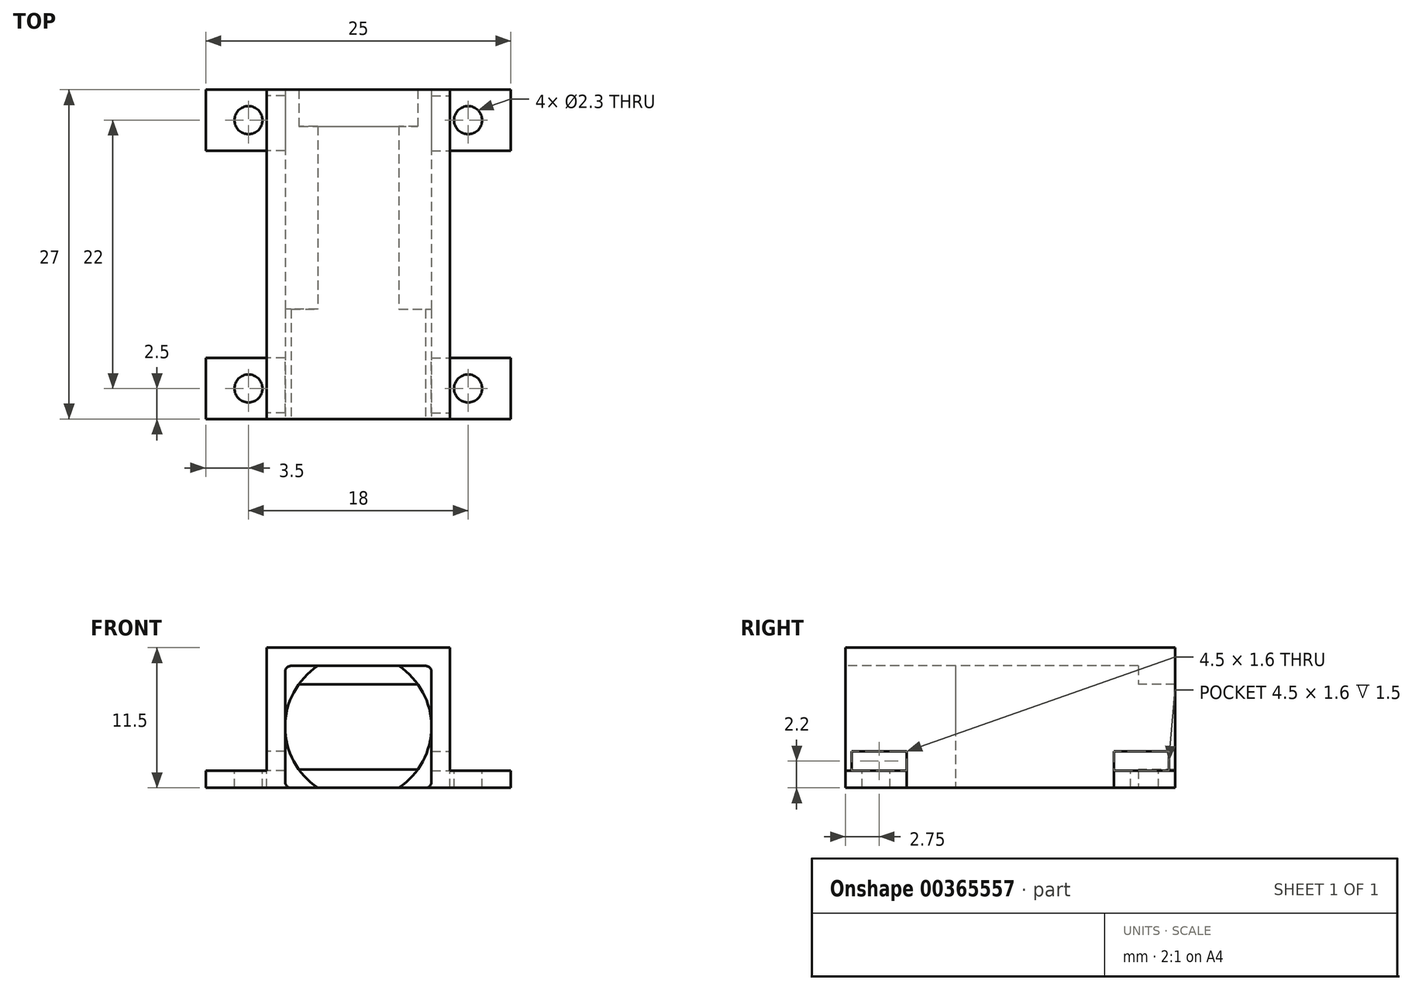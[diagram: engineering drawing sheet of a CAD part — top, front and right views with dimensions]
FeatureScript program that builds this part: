
annotation { "Feature Type Name" : "Feature", "Feature Type Description" : "" }
export const myFeature = defineFeature(function(context is Context, id is Id, definition is map)
    precondition{}
    {
        {
            var Q0;
            Q0=qCreatedBy(makeId("Front.planeOp"),FACE);
            var sketch = newSketch(context, id + "F0", { "sketchPlane" : qUnion([Q0])});
            skLineSegment(sketch, "E0", {"start": v(7.5, -5) * mm, "end": v(7.5, 6.5) * mm});
            skLineSegment(sketch, "E1", {"start": v(7.5, 6.5) * mm, "end": v(-7.5, 6.5) * mm});
            skLineSegment(sketch, "E2", {"start": v(-7.5, 6.5) * mm, "end": v(-7.5, -5) * mm});
            skPoint(sketch, "E3", {"position": v(0, -5) * mm});
            skLineSegment(sketch, "E4", {"start": v(-7.5, -5) * mm, "end": v(7.5, -5) * mm});
            skSolve(sketch);
        }
        {
            var Q0;
            Q0=makeQuery(id+"F0.imprint","IMPRINT",FACE,{"disambiguationData":[TD([[makeQuery(id+"F0.imprint","IMPRINT",EDGE,{"derivedFrom":sQuery(id+"F0.wireOp",EDGE,"E0")}),1.0]])]});
            extrude(context, id + "F1", {"entities" : qUnion([Q0]), "oppositeDirection" : true, "depth" : 27 * mm, "offsetDistance" : 25 * mm});
        }
        {
            var Q0;
            Q0=qCreatedBy(makeId("Front.planeOp"),FACE);
            var sketch = newSketch(context, id + "F2", { "sketchPlane" : qUnion([Q0])});
            skLineSegment(sketch, "E5.bottom", {"start": v(-5.5, 5) * mm, "end": v(5.5, 5) * mm});
            skLineSegment(sketch, "E5.top", {"start": v(-5.5, -5) * mm, "end": v(5.5, -5) * mm});
            skLineSegment(sketch, "E5.left", {"start": v(-6, 4.5) * mm, "end": v(-6, -4.5) * mm});
            skLineSegment(sketch, "E5.right", {"start": v(6, 4.5) * mm, "end": v(6, -4.5) * mm});
            skPoint(sketch, "E5.middle", {"position": v(0, 0) * mm});
            skPoint(sketch, "E6.visualSharp", {"position": v(-6, 5) * mm});
            skArc(sketch, "E6.filletArc", {"start": v(-5.5, 5) * mm, "mid": v(-5.85, 4.85) * mm, "end": v(-6, 4.5) * mm});
            skPoint(sketch, "E7.visualSharp", {"position": v(6, 5) * mm});
            skArc(sketch, "E7.filletArc", {"start": v(6, 4.5) * mm, "mid": v(5.85, 4.85) * mm, "end": v(5.5, 5) * mm});
            skPoint(sketch, "E8.visualSharp", {"position": v(6, -5) * mm});
            skArc(sketch, "E8.filletArc", {"start": v(5.5, -5) * mm, "mid": v(5.85, -4.85) * mm, "end": v(6, -4.5) * mm});
            skPoint(sketch, "E9.visualSharp", {"position": v(-6, -5) * mm});
            skArc(sketch, "E9.filletArc", {"start": v(-6, -4.5) * mm, "mid": v(-5.85, -4.85) * mm, "end": v(-5.5, -5) * mm});
            skSolve(sketch);
        }
        {
            var Q0;
            Q0=makeQuery(id+"F2.imprint","IMPRINT",FACE,{"disambiguationData":[TD([[makeQuery(id+"F2.imprint","IMPRINT",EDGE,{"derivedFrom":sQuery(id+"F2.wireOp",EDGE,"E5.bottom")}),-1.0]])]});
            extrude(context, id + "F3", {"entities" : qUnion([Q0]), "operationType" : NewBodyOperationType.REMOVE, "oppositeDirection" : true, "depth" : 9 * mm, "offsetDistance" : 25 * mm});
        }
        {
            var Q0;
            Q0=makeQuery(id+"F3.boolean.opBoolean","COPY",FACE,{"derivedFrom":makeQuery(id+"F3.opExtrude","CAP_FACE",FACE,{"disambiguationData":[OSD([sQuery(id+"F2.wireOp",EDGE,"E5.bottom"),sQuery(id+"F2.wireOp",EDGE,"E5.top"),sQuery(id+"F2.wireOp",EDGE,"E5.left"),sQuery(id+"F2.wireOp",EDGE,"E5.right"),sQuery(id+"F2.wireOp",EDGE,"E6.filletArc"),sQuery(id+"F2.wireOp",EDGE,"E7.filletArc"),sQuery(id+"F2.wireOp",EDGE,"E8.filletArc"),sQuery(id+"F2.wireOp",EDGE,"E9.filletArc")])],"isStart":false})});
            var sketch = newSketch(context, id + "F4", { "sketchPlane" : qUnion([Q0])});
            skArc(sketch, "E10", {"start": v(3.32, -5) * mm, "mid": v(6, 0) * mm, "end": v(3.32, 5) * mm});
            skLineSegment(sketch, "E11", {"start": v(0, 0) * mm, "end": v(0, 5) * mm});
            skLineSegment(sketch, "E12", {"start": v(-3.32, 5) * mm, "end": v(3.32, 5) * mm});
            skLineSegment(sketch, "E13.MirrorCS", {"start": v(-3.32, -5) * mm, "end": v(3.32, -5) * mm});
            skArc(sketch, "E14.trimOffspring", {"start": v(-3.32, 5) * mm, "mid": v(-6, 0) * mm, "end": v(-3.32, -5) * mm});
            skSolve(sketch);
        }
        {
            var Q0;
            {var subQ2=makeQuery(id+"F3.opExtrude","CAP_EDGE",EDGE,{"disambiguationData":[OSD([sQuery(id+"F2.wireOp",EDGE,"E5.top")])],"isStart":false});var subQ6=sQuery(id+"F4.wireOp",EDGE,"E10");var subQ7=makeQuery(id+"F4.imprint","INTERSECT",VERTEX,{"derivedFrom":[subQ2,subQ6]});Q0=makeQuery(id+"F4.imprint","IMPRINT",FACE,{"disambiguationData":[TD([[makeQuery(id+"F4.imprint","IMPRINT",EDGE,{"disambiguationData":[TD([[subQ7,-1.0]])],"derivedFrom":subQ6}),1.0]])]});}
            var Q1;
            {var subQ0=sQuery(id+"F4.wireOp",EDGE,"E13.MirrorCS");Q1=makeQuery(id+"F4.imprint","IMPRINT",FACE,{"disambiguationData":[TD([[makeQuery(id+"F4.imprint","IMPRINT",EDGE,{"derivedFrom":subQ0}),1.0]])]});}
            var Q2;
            {var subQ0=sQuery(id+"F4.wireOp",EDGE,"E12");var subQ1=sQuery(id+"F4.wireOp",EDGE,"E10");var subQ2=makeQuery(id+"F4.imprint","INTERSECT",VERTEX,{"derivedFrom":[subQ1,subQ0]});Q2=makeQuery(id+"F4.imprint","IMPRINT",FACE,{"disambiguationData":[TD([[makeQuery(id+"F4.imprint","IMPRINT",EDGE,{"disambiguationData":[TD([[subQ2,1.0]])],"derivedFrom":subQ1}),1.0]])]});}
            var Q3;
            {var subQ0=sQuery(id+"F4.wireOp",EDGE,"E12");var subQ1=sQuery(id+"F4.wireOp",EDGE,"E11");var subQ2=makeQuery(id+"F4.imprint","INTERSECT",VERTEX,{"derivedFrom":[subQ1,subQ0]});Q3=makeQuery(id+"F4.imprint","IMPRINT",FACE,{"disambiguationData":[TD([[makeQuery(id+"F4.imprint","IMPRINT",EDGE,{"disambiguationData":[TD([[subQ2,1.0]])],"derivedFrom":subQ1}),1.0]])]});}
            extrude(context, id + "F5", {"entities" : qUnion([Q0, Q1, Q2, Q3]), "operationType" : NewBodyOperationType.REMOVE, "oppositeDirection" : true, "depth" : 15 * mm, "offsetDistance" : 25 * mm});
        }
        {
            var Q0;
            Q0=makeQuery(id+"F5.boolean.opBoolean","COPY",FACE,{"derivedFrom":makeQuery(id+"F5.opExtrude","CAP_FACE",FACE,{"disambiguationData":[OSD([sQuery(id+"F4.wireOp",EDGE,"E10"),sQuery(id+"F4.wireOp",EDGE,"E12"),sQuery(id+"F4.wireOp",EDGE,"E13.MirrorCS"),sQuery(id+"F4.wireOp",EDGE,"E14.trimOffspring")])],"isStart":false})});
            var sketch = newSketch(context, id + "F6", { "sketchPlane" : qUnion([Q0])});
            skCircle(sketch, "E15", {"center": v(0, 0) * mm, "radius": 6 * mm});
            skLineSegment(sketch, "E16", {"start": v(0, 0) * mm, "end": v(0, 3.5) * mm});
            skPoint(sketch, "E16.endSnap0", {"position": v(0, 5) * mm});
            skLineSegment(sketch, "E17", {"start": v(-4.87, 3.5) * mm, "end": v(4.87, 3.5) * mm});
            skLineSegment(sketch, "E18.MirrorCS", {"start": v(-4.87, -3.5) * mm, "end": v(4.87, -3.5) * mm});
            skSolve(sketch);
        }
        {
            var Q0;
            {var subQ5=sQuery(id+"F6.wireOp",EDGE,"E18.MirrorCS");Q0=makeQuery(id+"F6.imprint","IMPRINT",FACE,{"disambiguationData":[TD([[makeQuery(id+"F6.imprint","IMPRINT",EDGE,{"derivedFrom":subQ5}),1.0]])]});}
            extrude(context, id + "F7", {"entities" : qUnion([Q0]), "operationType" : NewBodyOperationType.REMOVE, "oppositeDirection" : true, "depth" : 3 * mm, "offsetDistance" : 25 * mm});
        }
        {
            var Q0;
            Q0=makeQuery(id+"F1.opExtrude","SWEPT_FACE",FACE,{"disambiguationData":[OSD([sQuery(id+"F0.wireOp",EDGE,"E0")])]});
            var sketch = newSketch(context, id + "F8", { "sketchPlane" : qUnion([Q0])});
            skLineSegment(sketch, "E19.bottom", {"start": v(0, -5) * mm, "end": v(5, -5) * mm});
            skLineSegment(sketch, "E19.top", {"start": v(0, -3.6) * mm, "end": v(5, -3.6) * mm});
            skLineSegment(sketch, "E19.left", {"start": v(0, -5) * mm, "end": v(0, -3.6) * mm});
            skLineSegment(sketch, "E19.right", {"start": v(5, -5) * mm, "end": v(5, -3.6) * mm});
            skLineSegment(sketch, "E20.bottom", {"start": v(27, -5) * mm, "end": v(22, -5) * mm});
            skLineSegment(sketch, "E20.top", {"start": v(27, -3.6) * mm, "end": v(22, -3.6) * mm});
            skLineSegment(sketch, "E20.left", {"start": v(27, -5) * mm, "end": v(27, -3.6) * mm});
            skLineSegment(sketch, "E20.right", {"start": v(22, -5) * mm, "end": v(22, -3.6) * mm});
            skSolve(sketch);
        }
        {
            var Q0;
            Q0=makeQuery(id+"F8.imprint","IMPRINT",FACE,{"disambiguationData":[TD([[makeQuery(id+"F8.imprint","IMPRINT",EDGE,{"derivedFrom":sQuery(id+"F8.wireOp",EDGE,"E19.bottom")}),-1.0]])]});
            var Q1;
            Q1=makeQuery(id+"F8.imprint","IMPRINT",FACE,{"disambiguationData":[TD([[makeQuery(id+"F8.imprint","IMPRINT",EDGE,{"derivedFrom":sQuery(id+"F8.wireOp",EDGE,"E20.bottom")}),-1.0]])]});
            extrude(context, id + "F9", {"entities" : qUnion([Q0, Q1]), "operationType" : NewBodyOperationType.ADD, "depth" : 5 * mm, "offsetDistance" : 25 * mm});
        }
        {
            var Q0;
            Q0=makeQuery(id+"F9.opExtrude","SWEPT_FACE",FACE,{"disambiguationData":[OSD([sQuery(id+"F8.wireOp",EDGE,"E20.top")])]});
            var sketch = newSketch(context, id + "F10", { "sketchPlane" : qUnion([Q0])});
            skPoint(sketch, "E21", {"position": v(7.5, 24.5) * mm});
            skLineSegment(sketch, "E22", {"start": v(7.5, 24.5) * mm, "end": v(9, 24.5) * mm, "construction": true});
            skPoint(sketch, "E22.endSnap0", {"position": v(12.5, 24.5) * mm});
            skCircle(sketch, "E23", {"center": v(9, 24.5) * mm, "radius": 1.15 * mm});
            skLineSegment(sketch, "E24", {"start": v(9, 24.5) * mm, "end": v(9, 2.5) * mm, "construction": true});
            skCircle(sketch, "E25", {"center": v(9, 2.5) * mm, "radius": 1.15 * mm});
            skSolve(sketch);
        }
        {
            var Q0;
            Q0=makeQuery(id+"F10.imprint","IMPRINT",FACE,{"disambiguationData":[TD([[makeQuery(id+"F10.imprint","IMPRINT",EDGE,{"derivedFrom":sQuery(id+"F10.wireOp",EDGE,"E23")}),1.0]])]});
            var Q1;
            Q1=makeQuery(id+"F10.imprint","IMPRINT",FACE,{"disambiguationData":[TD([[makeQuery(id+"F10.imprint","IMPRINT",EDGE,{"derivedFrom":sQuery(id+"F10.wireOp",EDGE,"E25")}),1.0]])]});
            extrude(context, id + "F11", {"entities" : qUnion([Q0, Q1]), "operationType" : NewBodyOperationType.REMOVE, "oppositeDirection" : true, "depth" : 1.4 * mm, "offsetDistance" : 25 * mm});
        }
        {
            var Q0;
            Q0=makeQuery(id+"F1.opExtrude","SWEPT_FACE",FACE,{"disambiguationData":[OSD([sQuery(id+"F0.wireOp",EDGE,"E0")])]});
            var sketch = newSketch(context, id + "F12", { "sketchPlane" : qUnion([Q0])});
            skLineSegment(sketch, "E26.bottom", {"start": v(0.5, -3.6) * mm, "end": v(5, -3.6) * mm});
            skLineSegment(sketch, "E26.top", {"start": v(0.5, -2) * mm, "end": v(5, -2) * mm});
            skLineSegment(sketch, "E26.left", {"start": v(0.5, -3.6) * mm, "end": v(0.5, -2) * mm});
            skLineSegment(sketch, "E26.right", {"start": v(5, -3.6) * mm, "end": v(5, -2) * mm});
            skLineSegment(sketch, "E27.bottom", {"start": v(22, -3.6) * mm, "end": v(26.5, -3.6) * mm});
            skLineSegment(sketch, "E27.top", {"start": v(22, -2) * mm, "end": v(26.5, -2) * mm});
            skLineSegment(sketch, "E27.left", {"start": v(22, -3.6) * mm, "end": v(22, -2) * mm});
            skLineSegment(sketch, "E27.right", {"start": v(26.5, -3.6) * mm, "end": v(26.5, -2) * mm});
            skSolve(sketch);
        }
        {
            var Q0;
            Q0=makeQuery(id+"F12.imprint","IMPRINT",FACE,{"disambiguationData":[TD([[makeQuery(id+"F12.imprint","IMPRINT",EDGE,{"derivedFrom":sQuery(id+"F12.wireOp",EDGE,"E26.bottom")}),1.0]])]});
            var Q1;
            Q1=makeQuery(id+"F12.imprint","IMPRINT",FACE,{"disambiguationData":[TD([[makeQuery(id+"F12.imprint","IMPRINT",EDGE,{"derivedFrom":sQuery(id+"F12.wireOp",EDGE,"YFqMWmTe-dDPr-wDUe-bICC-50DzHAynYKXx.bottom")}),-1.0]])]});
            var Q2;
            Q2=makeQuery(id+"F12.imprint","IMPRINT",FACE,{"disambiguationData":[TD([[makeQuery(id+"F12.imprint","IMPRINT",EDGE,{"derivedFrom":sQuery(id+"F12.wireOp",EDGE,"E27.bottom")}),-1.0]])]});
            extrude(context, id + "F13", {"entities" : qUnion([Q0, Q1, Q2]), "operationType" : NewBodyOperationType.REMOVE, "oppositeDirection" : true, "depth" : 1.5 * mm, "offsetDistance" : 25 * mm});
        }
        {
            var Q0;
            Q0=makeQuery(id+"F1.opExtrude","SWEPT_FACE",FACE,{"disambiguationData":[OSD([sQuery(id+"F0.wireOp",EDGE,"E2")])]});
            var sketch = newSketch(context, id + "F14", { "sketchPlane" : qUnion([Q0])});
            skLineSegment(sketch, "E28.bottom", {"start": v(-27, -5) * mm, "end": v(-22, -5) * mm});
            skLineSegment(sketch, "E28.top", {"start": v(-27, -3.6) * mm, "end": v(-22, -3.6) * mm});
            skLineSegment(sketch, "E28.left", {"start": v(-27, -5) * mm, "end": v(-27, -3.6) * mm});
            skLineSegment(sketch, "E28.right", {"start": v(-22, -5) * mm, "end": v(-22, -3.6) * mm});
            skLineSegment(sketch, "E29.bottom", {"start": v(0, -5) * mm, "end": v(-5, -5) * mm});
            skLineSegment(sketch, "E29.top", {"start": v(0, -3.6) * mm, "end": v(-5, -3.6) * mm});
            skLineSegment(sketch, "E29.left", {"start": v(0, -5) * mm, "end": v(0, -3.6) * mm});
            skLineSegment(sketch, "E29.right", {"start": v(-5, -5) * mm, "end": v(-5, -3.6) * mm});
            skSolve(sketch);
        }
        {
            var Q0;
            Q0=makeQuery(id+"F14.imprint","IMPRINT",FACE,{"disambiguationData":[TD([[makeQuery(id+"F14.imprint","IMPRINT",EDGE,{"derivedFrom":sQuery(id+"F14.wireOp",EDGE,"E28.bottom")}),1.0]])]});
            var Q1;
            Q1=makeQuery(id+"F14.imprint","IMPRINT",FACE,{"disambiguationData":[TD([[makeQuery(id+"F14.imprint","IMPRINT",EDGE,{"derivedFrom":sQuery(id+"F14.wireOp",EDGE,"E29.bottom")}),1.0]])]});
            extrude(context, id + "F15", {"entities" : qUnion([Q0, Q1]), "operationType" : NewBodyOperationType.ADD, "depth" : 5 * mm, "offsetDistance" : 25 * mm});
        }
        {
            var Q0;
            Q0=makeQuery(id+"F15.opExtrude","SWEPT_FACE",FACE,{"disambiguationData":[OSD([sQuery(id+"F14.wireOp",EDGE,"E28.top")])]});
            var sketch = newSketch(context, id + "F16", { "sketchPlane" : qUnion([Q0])});
            skLineSegment(sketch, "E30", {"start": v(-7.5, 24.5) * mm, "end": v(-9, 24.5) * mm, "construction": true});
            skLineSegment(sketch, "E31", {"start": v(-9, 24.5) * mm, "end": v(-9, 2.5) * mm, "construction": true});
            skCircle(sketch, "E32", {"center": v(-9, 24.5) * mm, "radius": 1.15 * mm});
            skCircle(sketch, "E33", {"center": v(-9, 2.5) * mm, "radius": 1.15 * mm});
            skSolve(sketch);
        }
        {
            var Q0;
            Q0=makeQuery(id+"F16.imprint","IMPRINT",FACE,{"disambiguationData":[TD([[makeQuery(id+"F16.imprint","IMPRINT",EDGE,{"derivedFrom":sQuery(id+"F16.wireOp",EDGE,"E33")}),1.0]])]});
            var Q1;
            Q1=makeQuery(id+"F16.imprint","IMPRINT",FACE,{"disambiguationData":[TD([[makeQuery(id+"F16.imprint","IMPRINT",EDGE,{"derivedFrom":sQuery(id+"F16.wireOp",EDGE,"E32")}),1.0]])]});
            extrude(context, id + "F17", {"entities" : qUnion([Q0, Q1]), "operationType" : NewBodyOperationType.REMOVE, "oppositeDirection" : true, "depth" : 1.4 * mm, "offsetDistance" : 25 * mm});
        }
        {
            var Q0;
            Q0=makeQuery(id+"F1.opExtrude","SWEPT_FACE",FACE,{"disambiguationData":[OSD([sQuery(id+"F0.wireOp",EDGE,"E2")])]});
            var sketch = newSketch(context, id + "F18", { "sketchPlane" : qUnion([Q0])});
            skLineSegment(sketch, "E34.bottom", {"start": v(-22, -3.6) * mm, "end": v(-26.5, -3.6) * mm});
            skLineSegment(sketch, "E34.top", {"start": v(-22, -2) * mm, "end": v(-26.5, -2) * mm});
            skLineSegment(sketch, "E34.left", {"start": v(-22, -3.6) * mm, "end": v(-22, -2) * mm});
            skLineSegment(sketch, "E34.right", {"start": v(-26.5, -3.6) * mm, "end": v(-26.5, -2) * mm});
            skLineSegment(sketch, "E35.bottom", {"start": v(-5, -3.6) * mm, "end": v(-0.5, -3.6) * mm});
            skLineSegment(sketch, "E35.top", {"start": v(-5, -2) * mm, "end": v(-0.5, -2) * mm});
            skLineSegment(sketch, "E35.left", {"start": v(-5, -3.6) * mm, "end": v(-5, -2) * mm});
            skLineSegment(sketch, "E35.right", {"start": v(-0.5, -3.6) * mm, "end": v(-0.5, -2) * mm});
            skSolve(sketch);
        }
        {
            var Q0;
            Q0=makeQuery(id+"F18.imprint","IMPRINT",FACE,{"disambiguationData":[TD([[makeQuery(id+"F18.imprint","IMPRINT",EDGE,{"derivedFrom":sQuery(id+"F18.wireOp",EDGE,"E34.bottom")}),1.0]])]});
            var Q1;
            Q1=makeQuery(id+"F18.imprint","IMPRINT",FACE,{"disambiguationData":[TD([[makeQuery(id+"F18.imprint","IMPRINT",EDGE,{"derivedFrom":sQuery(id+"F18.wireOp",EDGE,"E35.bottom")}),-1.0]])]});
            extrude(context, id + "F19", {"entities" : qUnion([Q0, Q1]), "operationType" : NewBodyOperationType.REMOVE, "oppositeDirection" : true, "depth" : 1.5 * mm, "offsetDistance" : 25 * mm});
        }
    });
